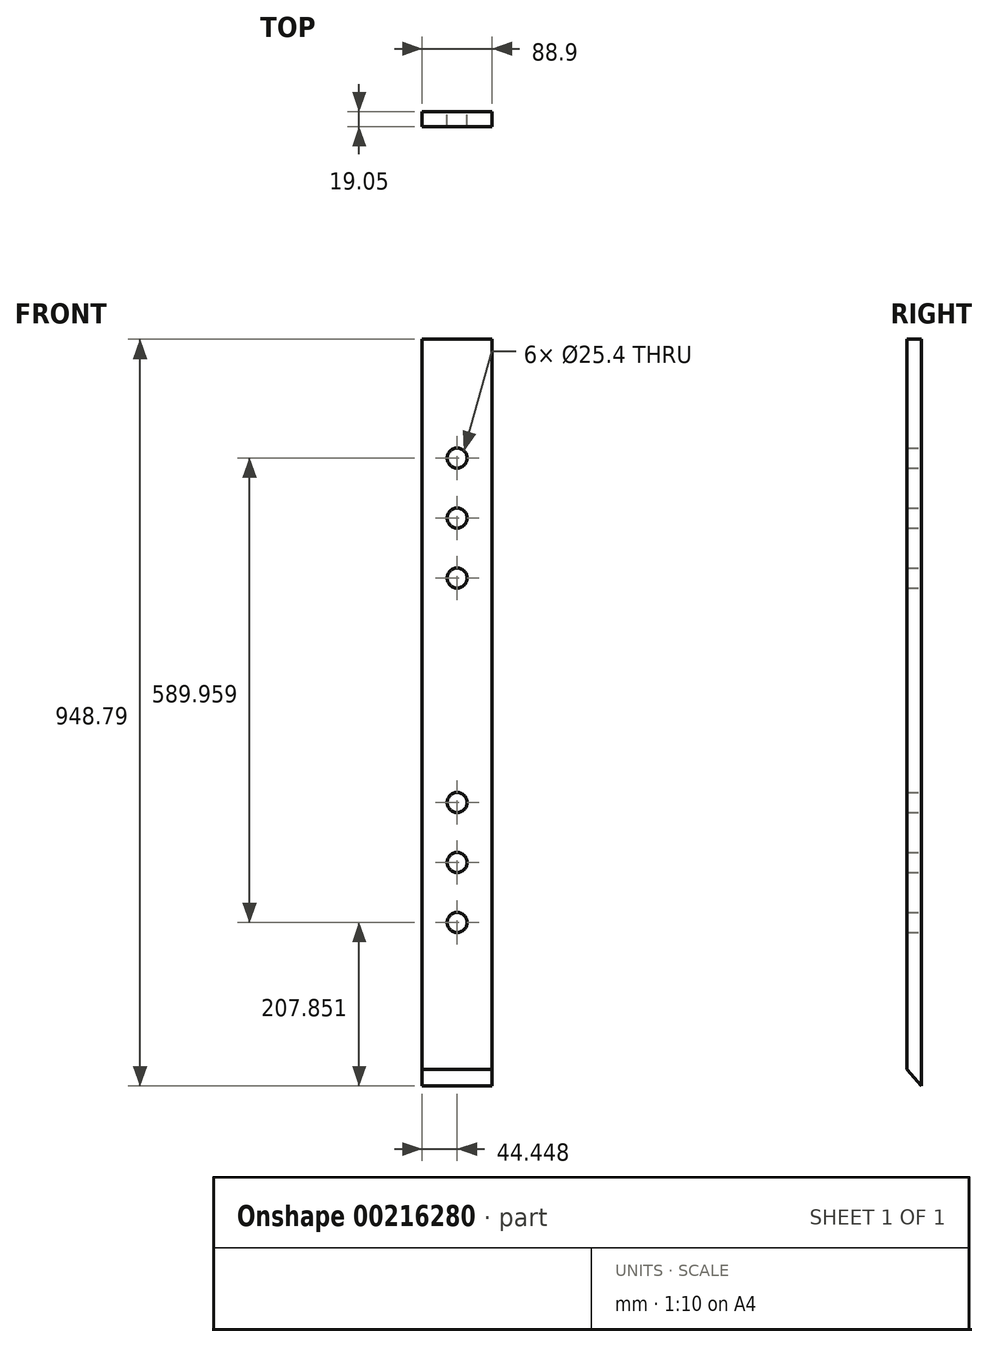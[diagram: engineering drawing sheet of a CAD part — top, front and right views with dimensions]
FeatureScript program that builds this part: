
annotation { "Feature Type Name" : "Feature", "Feature Type Description" : "" }
export const myFeature = defineFeature(function(context is Context, id is Id, definition is map)
    precondition{}
    {
        {
            var Q0;
            Q0=qCreatedBy(makeId("Front.planeOp"),FACE);
            var sketch = newSketch(context, id + "F0", { "sketchPlane" : qUnion([Q0])});
            skLineSegment(sketch, "E0", {"start": v(707.46, 3633.57) * mm, "end": v(796.36, 3633.57) * mm});
            skLineSegment(sketch, "E1", {"start": v(796.36, 3633.57) * mm, "end": v(796.36, 2684.25) * mm});
            skLineSegment(sketch, "E2", {"start": v(796.36, 2684.78) * mm, "end": v(707.46, 2684.78) * mm});
            skLineSegment(sketch, "E3", {"start": v(707.46, 2684.78) * mm, "end": v(707.46, 3634.1) * mm});
            skCircle(sketch, "E4", {"center": v(751.9, 2892.63) * mm, "radius": 12.7 * mm});
            skCircle(sketch, "E5", {"center": v(751.9, 2968.83) * mm, "radius": 12.7 * mm});
            skCircle(sketch, "E6", {"center": v(751.9, 3045.03) * mm, "radius": 12.7 * mm});
            skCircle(sketch, "E7", {"center": v(751.9, 3330.19) * mm, "radius": 12.7 * mm});
            skCircle(sketch, "E8", {"center": v(751.9, 3406.39) * mm, "radius": 12.7 * mm});
            skCircle(sketch, "E9", {"center": v(751.9, 3482.59) * mm, "radius": 12.7 * mm});
            skLineSegment(sketch, "E10", {"start": v(751.9, 2684.78) * mm, "end": v(751.9, 3633.57) * mm, "construction": true});
            skSolve(sketch);
        }
        {
            var Q0;
            {var subQ1=sQuery(id+"F0.wireOp",EDGE,"E0");Q0=makeQuery(id+"F0.imprint","IMPRINT",FACE,{"disambiguationData":[TD([[makeQuery(id+"F0.imprint","IMPRINT",EDGE,{"derivedFrom":subQ1}),-1.0]])]});}
            extrude(context, id + "F1", {"entities" : qUnion([Q0]), "depth" : 19.05 * mm});
        }
        {
            var Q0;
            Q0=makeQuery(id+"F1.opExtrude","SWEPT_FACE",FACE,{"disambiguationData":[OSD([sQuery(id+"F0.wireOp",EDGE,"E1")])]});
            var sketch = newSketch(context, id + "F2", { "sketchPlane" : qUnion([Q0])});
            skLineSegment(sketch, "E11", {"start": v(0, 2684.78) * mm, "end": v(-19.05, 2684.78) * mm});
            skLineSegment(sketch, "E12", {"start": v(-19.05, 2684.78) * mm, "end": v(-19.05, 2705.98) * mm});
            skLineSegment(sketch, "E13", {"start": v(-19.05, 2705.98) * mm, "end": v(0, 2684.78) * mm});
            skSolve(sketch);
        }
        {
            var Q0;
            Q0=makeQuery(id+"F2.imprint","IMPRINT",FACE,{"disambiguationData":[TD([[makeQuery(id+"F2.imprint","IMPRINT",EDGE,{"derivedFrom":sQuery(id+"F2.wireOp",EDGE,"E11")}),1.0]])]});
            extrude(context, id + "F3", {"entities" : qUnion([Q0]), "operationType" : NewBodyOperationType.REMOVE, "endBound" : BoundingType.THROUGH_ALL, "oppositeDirection" : true, "depth" : 25.4 * mm});
        }
    });
